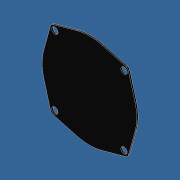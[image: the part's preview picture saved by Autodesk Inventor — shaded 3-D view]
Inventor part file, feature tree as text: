
AUTODESK INVENTOR PART (.ipt)
format: ipt  version: unknown  size: 185,344 bytes
history: native  units: in
note: dims shown in document units (in); Inventor stores cm internally (conversion verified against a paired STEP export)
features: extrude x1, sketch x1
ambient origin geometry x8: Origin, YZ Plane, XZ Plane, XY Plane, X Axis, Y Axis, Z Axis, Center Point
bodies: Solid1 (feature_tree)
feature tree (2):
  extrude  "Extrusion1"  [1 undecoded]
  sketch  "Sketch1"  dims[d0=0.05in d1=0.0in]
note: 1 required parameter value undecoded (feature->parameter linkage not recoverable at this tier; creation-order binding heuristic only, values carry confidence <= 0.55)
